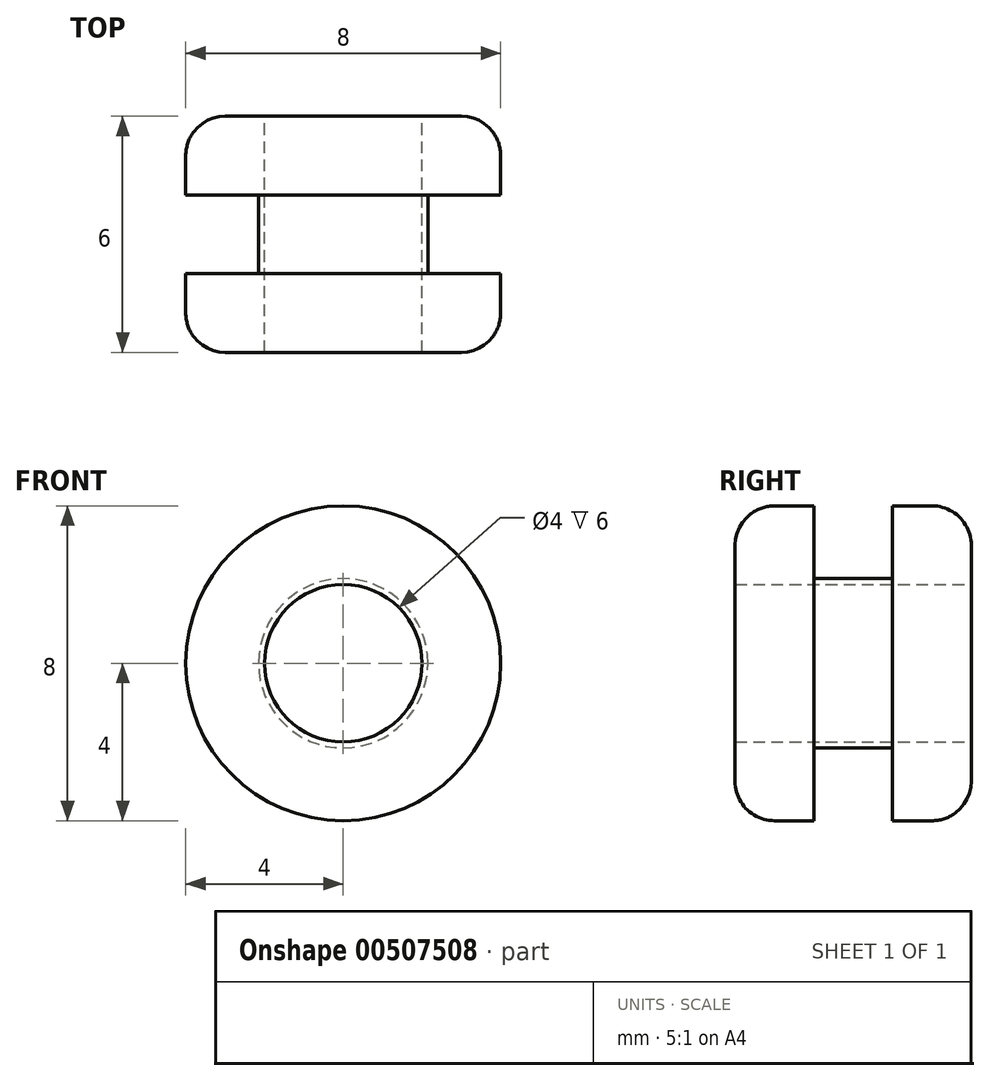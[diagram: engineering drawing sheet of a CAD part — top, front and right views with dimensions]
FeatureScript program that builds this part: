
annotation { "Feature Type Name" : "Feature", "Feature Type Description" : "" }
export const myFeature = defineFeature(function(context is Context, id is Id, definition is map)
    precondition{}
    {
        {
            var Q0;
            Q0=qCreatedBy(makeId("Front.planeOp"),FACE);
            var sketch = newSketch(context, id + "F0", { "sketchPlane" : qUnion([Q0])});
            skCircle(sketch, "E0", {"center": v(0, 0) * mm, "radius": 4 * mm});
            skSolve(sketch);
        }
        {
            var Q0;
            Q0=qSketchRegion(id+"F0",true);
            extrude(context, id + "F1", {"entities" : qUnion([Q0]), "depth" : 2 * mm});
        }
        {
            var Q0;
            Q0=makeQuery(id+"F1.opExtrude","CAP_EDGE",EDGE,{"disambiguationData":[OSD([sQuery(id+"F0.wireOp",EDGE,"E0")])],"isStart":false});
            fillet(context, id + "F2", {"entities" : qUnion([Q0]), "radius" : 1 * mm, "tangentPropagation" : true, "allowEdgeOverflow" : false});
        }
        {
            var Q0;
            Q0=makeQuery(id+"F1.opExtrude","CAP_FACE",FACE,{"disambiguationData":[OSD([sQuery(id+"F0.wireOp",EDGE,"E0")])],"isStart":true});
            var sketch = newSketch(context, id + "F3", { "sketchPlane" : qUnion([Q0])});
            skCircle(sketch, "E1", {"center": v(0, 0) * mm, "radius": 2.15 * mm});
            skSolve(sketch);
        }
        {
            var Q0;
            Q0=qSketchRegion(id+"F3",true);
            extrude(context, id + "F4", {"entities" : qUnion([Q0]), "operationType" : NewBodyOperationType.ADD, "depth" : 2 * mm});
        }
        {
            var Q0;
            Q0=makeQuery(id+"F4.opExtrude","CAP_FACE",FACE,{"disambiguationData":[OSD([sQuery(id+"F3.wireOp",EDGE,"E1")])],"isStart":false});
            var sketch = newSketch(context, id + "F5", { "sketchPlane" : qUnion([Q0])});
            skCircle(sketch, "E2", {"center": v(0, 0) * mm, "radius": 4 * mm});
            skSolve(sketch);
        }
        {
            var Q0;
            Q0=qSketchRegion(id+"F5",true);
            extrude(context, id + "F6", {"entities" : qUnion([Q0]), "operationType" : NewBodyOperationType.ADD, "depth" : 2 * mm});
        }
        {
            var Q0;
            Q0=makeQuery(id+"F6.opExtrude","CAP_EDGE",EDGE,{"disambiguationData":[OSD([sQuery(id+"F5.wireOp",EDGE,"E2")])],"isStart":false});
            fillet(context, id + "F7", {"entities" : qUnion([Q0]), "radius" : 1 * mm, "tangentPropagation" : true, "allowEdgeOverflow" : false});
        }
        {
            var Q0;
            Q0=makeQuery(id+"F6.opExtrude","CAP_FACE",FACE,{"disambiguationData":[OSD([sQuery(id+"F5.wireOp",EDGE,"E2")])],"isStart":false});
            var sketch = newSketch(context, id + "F8", { "sketchPlane" : qUnion([Q0])});
            skCircle(sketch, "E3", {"center": v(0, 0) * mm, "radius": 2 * mm});
            skSolve(sketch);
        }
        {
            var Q0;
            Q0=qSketchRegion(id+"F8",true);
            extrude(context, id + "F9", {"entities" : qUnion([Q0]), "operationType" : NewBodyOperationType.REMOVE, "oppositeDirection" : true, "depth" : 6 * mm});
        }
    });
